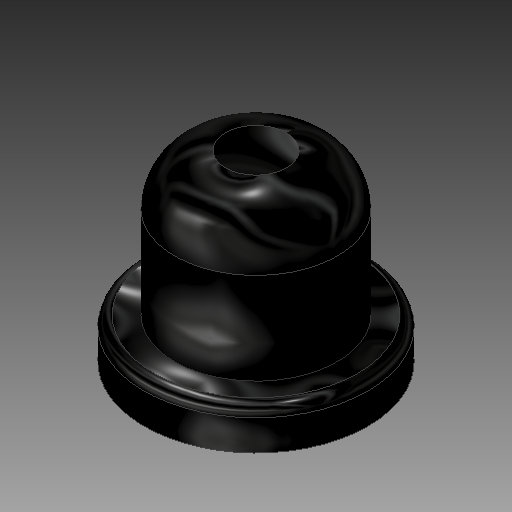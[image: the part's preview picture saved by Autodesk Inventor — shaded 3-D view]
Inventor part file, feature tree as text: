
AUTODESK INVENTOR PART (.ipt)
format: ipt  version: 2019 (Build 230136000, 136)  size: 228,352 bytes
history: native  units: mm
features: sketch x4, extrude x3, fillet x2, other x1, shell x1
ambient origin geometry x8: Origin, YZ Plane, XZ Plane, XY Plane, X Axis, Y Axis, Z Axis, Center Point
bodies: Solide1 (feature_tree)
feature tree (11):
  other  "Button"
  extrude  "Extrusion1"  Depth=8.0mm
  fillet  "Congé1"  Radius=7.0mm
  extrude  "Extrusion2"  Depth=2.5mm
  sketch  "Esquisse3"
  shell  "Coque1"  Thickness=11.0mm
  extrude  "Extrusion3"  Depth=2.0mm TaperAngle=0.0deg
  fillet  "Congé2"  Radius=1.2mm
  sketch  "Esquisse1"
  sketch  "Esquisse2"
  sketch  "Esquisse4"
